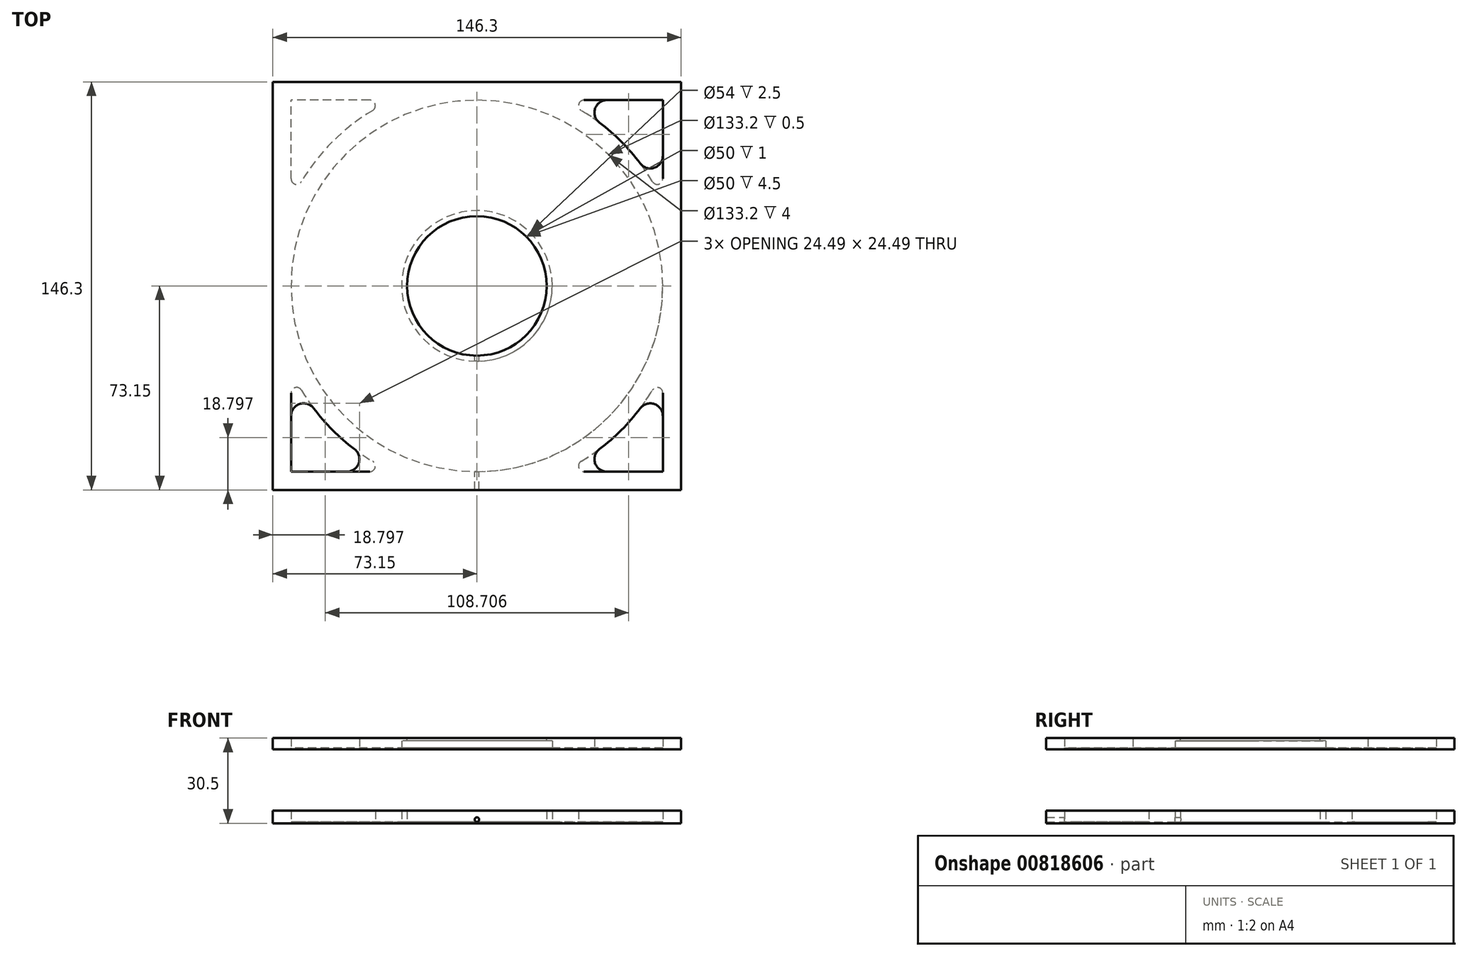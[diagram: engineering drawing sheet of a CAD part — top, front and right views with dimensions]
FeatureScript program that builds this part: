
annotation { "Feature Type Name" : "Feature", "Feature Type Description" : "" }
export const myFeature = defineFeature(function(context is Context, id is Id, definition is map)
    precondition{}
    {
        {
            var Q0;
            Q0=qCreatedBy(makeId("Top.planeOp"),FACE);
            var sketch = newSketch(context, id + "F0", { "sketchPlane" : qUnion([Q0])});
            skLineSegment(sketch, "E0.bottom", {"start": v(-73.15, 73.15) * mm, "end": v(73.15, 73.15) * mm});
            skLineSegment(sketch, "E0.top", {"start": v(-73.15, -73.15) * mm, "end": v(73.15, -73.15) * mm});
            skLineSegment(sketch, "E0.left", {"start": v(-73.15, 73.15) * mm, "end": v(-73.15, -73.15) * mm});
            skLineSegment(sketch, "E0.right", {"start": v(73.15, 73.15) * mm, "end": v(73.15, -73.15) * mm});
            skLineSegment(sketch, "E1", {"start": v(-73.15, 0) * mm, "end": v(73.15, 0) * mm, "construction": true});
            skPoint(sketch, "E2", {"position": v(0, 73.15) * mm});
            skLineSegment(sketch, "E3", {"start": v(0, 73.15) * mm, "end": v(0, -73.15) * mm, "construction": true});
            skPoint(sketch, "E4", {"position": v(0, 0) * mm});
            skCircle(sketch, "E5", {"center": v(0, 0) * mm, "radius": 25 * mm});
            skSolve(sketch);
        }
        {
            var Q0;
            Q0=makeQuery(id+"F0.imprint","IMPRINT",FACE,{"disambiguationData":[TD([[makeQuery(id+"F0.imprint","IMPRINT",EDGE,{"derivedFrom":sQuery(id+"F0.wireOp",EDGE,"E0.bottom")}),-1.0]])]});
            extrude(context, id + "F1", {"entities" : qUnion([Q0]), "depth" : .5 * mm, "offsetDistance" : 25 * mm});
        }
        {
            var Q0;
            Q0=makeQuery(id+"F1.opExtrude","CAP_FACE",FACE,{"disambiguationData":[OSD([sQuery(id+"F0.wireOp",EDGE,"E0.bottom"),sQuery(id+"F0.wireOp",EDGE,"E0.top"),sQuery(id+"F0.wireOp",EDGE,"E0.left"),sQuery(id+"F0.wireOp",EDGE,"E0.right"),sQuery(id+"F0.wireOp",EDGE,"E5")])],"isStart":false});
            var sketch = newSketch(context, id + "F2", { "sketchPlane" : qUnion([Q0])});
            skCircle(sketch, "E6", {"center": v(0, 0) * mm, "radius": 27 * mm});
            skCircle(sketch, "E7", {"center": v(0, 0) * mm, "radius": 66.6 * mm});
            skArc(sketch, "E8", {"start": v(-37.38, 62.88) * mm, "mid": v(-51.72, 51.72) * mm, "end": v(-62.88, 37.38) * mm});
            skLineSegment(sketch, "E9", {"start": v(-66.6, 38.4) * mm, "end": v(-66.6, 66.6) * mm});
            skPoint(sketch, "E9.startSnap0", {"position": v(-73.15, 0) * mm});
            skLineSegment(sketch, "E10", {"start": v(-38.4, 66.6) * mm, "end": v(-66.6, 66.6) * mm});
            skPoint(sketch, "E11.orphan", {"position": v(-66.6, 0) * mm});
            skPoint(sketch, "E12.orphan", {"position": v(0, 66.6) * mm});
            skLineSegment(sketch, "E13.1.0", {"start": v(-38.4, -66.6) * mm, "end": v(-66.6, -66.6) * mm});
            skArc(sketch, "E13.1.1", {"start": v(-62.88, -37.38) * mm, "mid": v(-51.72, -51.72) * mm, "end": v(-37.38, -62.88) * mm});
            skLineSegment(sketch, "E13.1.2", {"start": v(-66.6, -38.4) * mm, "end": v(-66.6, -66.6) * mm});
            skLineSegment(sketch, "E13.2.0", {"start": v(66.6, -38.4) * mm, "end": v(66.6, -66.6) * mm});
            skArc(sketch, "E13.2.1", {"start": v(37.38, -62.88) * mm, "mid": v(51.72, -51.72) * mm, "end": v(62.88, -37.38) * mm});
            skLineSegment(sketch, "E13.2.2", {"start": v(38.4, -66.6) * mm, "end": v(66.6, -66.6) * mm});
            skLineSegment(sketch, "E13.3.0", {"start": v(38.4, 66.6) * mm, "end": v(66.6, 66.6) * mm});
            skArc(sketch, "E13.3.1", {"start": v(62.88, 37.38) * mm, "mid": v(51.72, 51.72) * mm, "end": v(37.38, 62.88) * mm});
            skLineSegment(sketch, "E13.3.2", {"start": v(66.6, 38.4) * mm, "end": v(66.6, 66.6) * mm});
            skPoint(sketch, "E14.visualSharp", {"position": v(-66.6, 30.25) * mm});
            skArc(sketch, "E14.filletArc", {"start": v(-66.6, 38.4) * mm, "mid": v(-65.13, 36.47) * mm, "end": v(-62.88, 37.38) * mm});
            skPoint(sketch, "E15.visualSharp", {"position": v(-30.25, 66.6) * mm});
            skArc(sketch, "E15.filletArc", {"start": v(-37.38, 62.88) * mm, "mid": v(-36.47, 65.13) * mm, "end": v(-38.4, 66.6) * mm});
            skPoint(sketch, "E16.visualSharp", {"position": v(30.25, 66.6) * mm});
            skArc(sketch, "E16.filletArc", {"start": v(38.4, 66.6) * mm, "mid": v(36.47, 65.13) * mm, "end": v(37.38, 62.88) * mm});
            skPoint(sketch, "E17.visualSharp", {"position": v(66.6, 30.25) * mm});
            skArc(sketch, "E17.filletArc", {"start": v(62.88, 37.38) * mm, "mid": v(65.13, 36.47) * mm, "end": v(66.6, 38.4) * mm});
            skPoint(sketch, "E18.visualSharp", {"position": v(66.6, -30.25) * mm});
            skArc(sketch, "E18.filletArc", {"start": v(66.6, -38.4) * mm, "mid": v(65.13, -36.47) * mm, "end": v(62.88, -37.38) * mm});
            skPoint(sketch, "E19.visualSharp", {"position": v(30.25, -66.6) * mm});
            skArc(sketch, "E19.filletArc", {"start": v(37.38, -62.88) * mm, "mid": v(36.47, -65.13) * mm, "end": v(38.4, -66.6) * mm});
            skPoint(sketch, "E20.visualSharp", {"position": v(-30.25, -66.6) * mm});
            skArc(sketch, "E20.filletArc", {"start": v(-38.4, -66.6) * mm, "mid": v(-36.47, -65.13) * mm, "end": v(-37.38, -62.88) * mm});
            skPoint(sketch, "E21.visualSharp", {"position": v(-66.6, -30.25) * mm});
            skArc(sketch, "E21.filletArc", {"start": v(-62.88, -37.38) * mm, "mid": v(-65.13, -36.47) * mm, "end": v(-66.6, -38.4) * mm});
            skSolve(sketch);
        }
        {
            var Q0;
            Q0=makeQuery(id+"F2.imprint","IMPRINT",FACE,{"disambiguationData":[TD([[makeQuery(id+"F2.imprint","IMPRINT",EDGE,{"derivedFrom":sQuery(id+"F2.wireOp",EDGE,"E7")}),-1.0]])]});
            extrude(context, id + "F3", {"entities" : qUnion([Q0]), "operationType" : NewBodyOperationType.ADD, "depth" : 4 * mm, "offsetDistance" : 25 * mm});
        }
        {
            var Q0;
            Q0=makeQuery(id+"F2.imprint","IMPRINT",FACE,{"disambiguationData":[TD([[makeQuery(id+"F2.imprint","IMPRINT",EDGE,{"derivedFrom":sQuery(id+"F2.wireOp",EDGE,"E6")}),1.0]])]});
            extrude(context, id + "F4", {"entities" : qUnion([Q0]), "operationType" : NewBodyOperationType.ADD, "depth" : 4 * mm, "offsetDistance" : 25 * mm});
        }
        {
            var Q0;
            Q0=qCreatedBy(makeId("Front.planeOp"),FACE);
            var sketch = newSketch(context, id + "F5", { "sketchPlane" : qUnion([Q0])});
            skCircle(sketch, "E22", {"center": v(0, 1.3) * mm, "radius": 0.8 * mm});
            skLineSegment(sketch, "E23.0", {"start": v(-66.6, 0.5) * mm, "end": v(66.6, 0.5) * mm, "construction": true});
            skSolve(sketch);
        }
        {
            var Q0;
            Q0=makeQuery(id+"F5.imprint","IMPRINT",FACE,{"disambiguationData":[TD([[makeQuery(id+"F5.imprint","IMPRINT",EDGE,{"derivedFrom":sQuery(id+"F5.wireOp",EDGE,"E22")}),1.0]])]});
            extrude(context, id + "F6", {"entities" : qUnion([Q0]), "operationType" : NewBodyOperationType.REMOVE, "endBound" : BoundingType.THROUGH_ALL, "depth" : 25 * mm, "offsetDistance" : 25 * mm});
        }
        {
            var Q0;
            Q0=makeQuery(id+"F3.opExtrude","CAP_FACE",FACE,{"disambiguationData":[OSD([sQuery(id+"F0.wireOp",EDGE,"E0.bottom"),sQuery(id+"F0.wireOp",EDGE,"E0.top"),sQuery(id+"F0.wireOp",EDGE,"E0.left"),sQuery(id+"F0.wireOp",EDGE,"E0.right"),sQuery(id+"F2.wireOp",EDGE,"E7")])],"isStart":false});
            cPlane(context, id + "F7", {"entities" : qUnion([Q0]), "cplaneType" : CPlaneType.OFFSET, "offset" : 25 * mm, "width" : 150 * mm, "height" : 150 * mm});
        }
        {
            var Q0;
            Q0=qCreatedBy(id+"F7.planeOp",FACE);
            var sketch = newSketch(context, id + "F8", { "sketchPlane" : qUnion([Q0])});
            skCircle(sketch, "E24.0", {"center": v(0, 0) * mm, "radius": 66.6 * mm});
            skCircle(sketch, "E24.1", {"center": v(0, 0) * mm, "radius": 27 * mm});
            skLineSegment(sketch, "E25.0", {"start": v(-73.15, 73.15) * mm, "end": v(73.15, 73.15) * mm});
            skLineSegment(sketch, "E25.1", {"start": v(-73.15, 73.15) * mm, "end": v(-73.15, -73.15) * mm});
            skLineSegment(sketch, "E25.2.0", {"start": v(73.15, 73.15) * mm, "end": v(-73.15, 73.15) * mm});
            skLineSegment(sketch, "E25.2.1", {"start": v(-73.15, 73.15) * mm, "end": v(-73.15, -73.15) * mm});
            skLineSegment(sketch, "E25.2.2", {"start": v(-73.15, -73.15) * mm, "end": v(73.15, -73.15) * mm});
            skLineSegment(sketch, "E25.2.3", {"start": v(73.15, -73.15) * mm, "end": v(73.15, 73.15) * mm});
            skLineSegment(sketch, "E26.0.1", {"start": v(-46.6, 66.6) * mm, "end": v(-66.6, 66.6) * mm});
            skLineSegment(sketch, "E26.0.2", {"start": v(-66.6, 66.6) * mm, "end": v(-66.6, 46.6) * mm});
            skArc(sketch, "E26.0.4", {"start": v(-58.51, 43.9) * mm, "mid": v(-51.72, 51.72) * mm, "end": v(-43.9, 58.51) * mm});
            skArc(sketch, "E27", {"start": v(-66.6, 46.6) * mm, "mid": v(-63.53, 42.34) * mm, "end": v(-58.51, 43.9) * mm});
            skArc(sketch, "E28", {"start": v(-43.9, 58.51) * mm, "mid": v(-42.34, 63.53) * mm, "end": v(-46.6, 66.6) * mm});
            skArc(sketch, "E29.1.0", {"start": v(-43.9, -58.51) * mm, "mid": v(-51.72, -51.72) * mm, "end": v(-58.51, -43.9) * mm});
            skArc(sketch, "E29.1.1", {"start": v(-58.51, -43.9) * mm, "mid": v(-63.53, -42.34) * mm, "end": v(-66.6, -46.6) * mm});
            skLineSegment(sketch, "E29.1.2", {"start": v(-66.6, -46.6) * mm, "end": v(-66.6, -66.6) * mm});
            skLineSegment(sketch, "E29.1.3", {"start": v(-66.6, -66.6) * mm, "end": v(-46.6, -66.6) * mm});
            skArc(sketch, "E29.1.4", {"start": v(-46.6, -66.6) * mm, "mid": v(-42.34, -63.53) * mm, "end": v(-43.9, -58.51) * mm});
            skArc(sketch, "E29.2.0", {"start": v(58.51, -43.9) * mm, "mid": v(51.72, -51.72) * mm, "end": v(43.9, -58.51) * mm});
            skArc(sketch, "E29.2.1", {"start": v(43.9, -58.51) * mm, "mid": v(42.34, -63.53) * mm, "end": v(46.6, -66.6) * mm});
            skLineSegment(sketch, "E29.2.2", {"start": v(46.6, -66.6) * mm, "end": v(66.6, -66.6) * mm});
            skLineSegment(sketch, "E29.2.3", {"start": v(66.6, -66.6) * mm, "end": v(66.6, -46.6) * mm});
            skArc(sketch, "E29.2.4", {"start": v(66.6, -46.6) * mm, "mid": v(63.53, -42.34) * mm, "end": v(58.51, -43.9) * mm});
            skArc(sketch, "E29.3.0", {"start": v(43.9, 58.51) * mm, "mid": v(51.72, 51.72) * mm, "end": v(58.51, 43.9) * mm});
            skArc(sketch, "E29.3.1", {"start": v(58.51, 43.9) * mm, "mid": v(63.53, 42.34) * mm, "end": v(66.6, 46.6) * mm});
            skLineSegment(sketch, "E29.3.2", {"start": v(66.6, 46.6) * mm, "end": v(66.6, 66.6) * mm});
            skLineSegment(sketch, "E29.3.3", {"start": v(66.6, 66.6) * mm, "end": v(46.6, 66.6) * mm});
            skArc(sketch, "E29.3.4", {"start": v(46.6, 66.6) * mm, "mid": v(42.34, 63.53) * mm, "end": v(43.9, 58.51) * mm});
            skSolve(sketch);
        }
        {
            var Q0;
            Q0=makeQuery(id+"F8.imprint","IMPRINT",FACE,{"disambiguationData":[TD([[makeQuery(id+"F8.imprint","IMPRINT",EDGE,{"derivedFrom":sQuery(id+"F8.wireOp",EDGE,"E24.0")}),-1.0]])]});
            var Q1;
            Q1=makeQuery(id+"F8.imprint","IMPRINT",FACE,{"disambiguationData":[TD([[makeQuery(id+"F8.imprint","IMPRINT",EDGE,{"derivedFrom":sQuery(id+"F8.wireOp",EDGE,"E26.0.1")}),1.0]])]});
            var Q2;
            Q2=makeQuery(id+"F8.imprint","IMPRINT",FACE,{"disambiguationData":[TD([[makeQuery(id+"F8.imprint","IMPRINT",EDGE,{"derivedFrom":sQuery(id+"F8.wireOp",EDGE,"E29.3.0")}),1.0]])]});
            var Q3;
            Q3=makeQuery(id+"F8.imprint","IMPRINT",FACE,{"disambiguationData":[TD([[makeQuery(id+"F8.imprint","IMPRINT",EDGE,{"derivedFrom":sQuery(id+"F8.wireOp",EDGE,"E29.2.0")}),1.0]])]});
            var Q4;
            Q4=makeQuery(id+"F8.imprint","IMPRINT",FACE,{"disambiguationData":[TD([[makeQuery(id+"F8.imprint","IMPRINT",EDGE,{"derivedFrom":sQuery(id+"F8.wireOp",EDGE,"E29.1.0")}),1.0]])]});
            var Q5;
            Q5=makeQuery(id+"F8.imprint","IMPRINT",FACE,{"disambiguationData":[TD([[makeQuery(id+"F8.imprint","IMPRINT",EDGE,{"derivedFrom":sQuery(id+"F8.wireOp",EDGE,"E24.0")}),1.0]])]});
            extrude(context, id + "F9", {"entities" : qUnion([Q0, Q1, Q2, Q3, Q4, Q5]), "depth" : 1 * mm, "offsetDistance" : 25 * mm});
        }
        {
            var Q0;
            Q0=makeQuery(id+"F8.imprint","IMPRINT",FACE,{"disambiguationData":[TD([[makeQuery(id+"F8.imprint","IMPRINT",EDGE,{"derivedFrom":sQuery(id+"F8.wireOp",EDGE,"E24.0")}),1.0]])]});
            extrude(context, id + "F10", {"entities" : qUnion([Q0]), "operationType" : NewBodyOperationType.ADD, "oppositeDirection" : true, "depth" : 2.5 * mm, "offsetDistance" : 25 * mm});
        }
        {
            var Q0;
            Q0=makeQuery(id+"F8.imprint","IMPRINT",FACE,{"disambiguationData":[TD([[makeQuery(id+"F8.imprint","IMPRINT",EDGE,{"derivedFrom":sQuery(id+"F8.wireOp",EDGE,"E29.1.0")}),1.0]])]});
            var Q1;
            Q1=makeQuery(id+"F8.imprint","IMPRINT",FACE,{"disambiguationData":[TD([[makeQuery(id+"F8.imprint","IMPRINT",EDGE,{"derivedFrom":sQuery(id+"F8.wireOp",EDGE,"E29.2.0")}),1.0]])]});
            var Q2;
            Q2=makeQuery(id+"F8.imprint","IMPRINT",FACE,{"disambiguationData":[TD([[makeQuery(id+"F8.imprint","IMPRINT",EDGE,{"derivedFrom":sQuery(id+"F8.wireOp",EDGE,"E26.0.1")}),1.0]])]});
            var Q3;
            Q3=makeQuery(id+"F8.imprint","IMPRINT",FACE,{"disambiguationData":[TD([[makeQuery(id+"F8.imprint","IMPRINT",EDGE,{"derivedFrom":sQuery(id+"F8.wireOp",EDGE,"E29.3.0")}),1.0]])]});
            extrude(context, id + "F11", {"entities" : qUnion([Q0, Q1, Q2, Q3]), "operationType" : NewBodyOperationType.ADD, "oppositeDirection" : true, "depth" : 3 * mm, "offsetDistance" : 25 * mm});
        }
        {
            var Q0;
            Q0=makeQuery(id+"F9.opExtrude","CAP_FACE",FACE,{"disambiguationData":[OSD([sQuery(id+"F8.wireOp",EDGE,"E24.1"),sQuery(id+"F8.wireOp",EDGE,"E25.2.0"),sQuery(id+"F8.wireOp",EDGE,"E25.2.1"),sQuery(id+"F8.wireOp",EDGE,"E25.2.2"),sQuery(id+"F8.wireOp",EDGE,"E25.2.3")])],"isStart":false});
            var sketch = newSketch(context, id + "F12", { "sketchPlane" : qUnion([Q0])});
            skCircle(sketch, "E30.0", {"center": v(0, 0) * mm, "radius": 27 * mm});
            skCircle(sketch, "E31", {"center": v(0, 0) * mm, "radius": 25 * mm});
            skSolve(sketch);
        }
        {
            var Q0;
            Q0=makeQuery(id+"F12.imprint","IMPRINT",FACE,{"disambiguationData":[TD([[makeQuery(id+"F12.imprint","IMPRINT",EDGE,{"derivedFrom":sQuery(id+"F12.wireOp",EDGE,"E30.0")}),1.0]])]});
            extrude(context, id + "F13", {"entities" : qUnion([Q0]), "operationType" : NewBodyOperationType.ADD, "oppositeDirection" : true, "depth" : 1 * mm, "offsetDistance" : 25 * mm});
        }
    });
